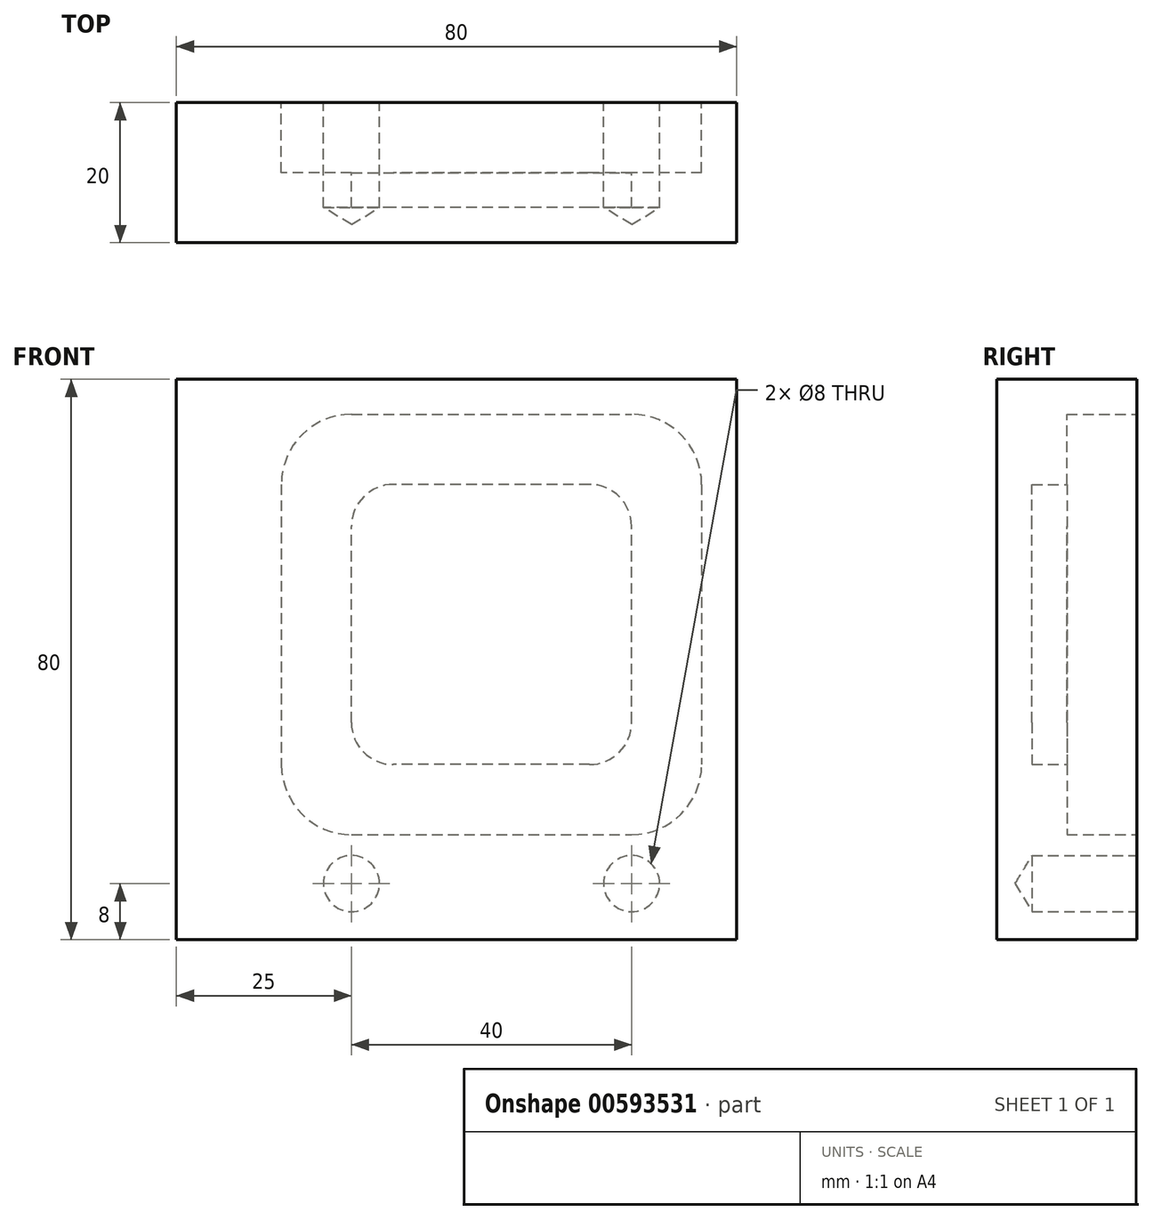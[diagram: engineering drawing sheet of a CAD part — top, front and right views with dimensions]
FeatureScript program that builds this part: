
annotation { "Feature Type Name" : "Feature", "Feature Type Description" : "" }
export const myFeature = defineFeature(function(context is Context, id is Id, definition is map)
    precondition{}
    {
        {
            var Q0;
            Q0=qCreatedBy(makeId("Front.planeOp"),FACE);
            var sketch = newSketch(context, id + "F0", { "sketchPlane" : qUnion([Q0])});
            skLineSegment(sketch, "E0", {"start": v(40, -40) * mm, "end": v(40, 40) * mm});
            skLineSegment(sketch, "E1", {"start": v(40, 40) * mm, "end": v(-40, 40) * mm});
            skLineSegment(sketch, "E2", {"start": v(-40, 40) * mm, "end": v(-40, -40) * mm});
            skLineSegment(sketch, "E3", {"start": v(-40, -40) * mm, "end": v(40, -40) * mm});
            skSolve(sketch);
        }
        {
            var Q0;
            Q0 = qSketchRegion(id + "F0", true);
            extrude(context, id + "F1", {"entities" : qUnion([Q0]), "depth" : 20 * mm, "offsetDistance" : 25 * mm});
        }
        {
            var Q0;
            Q0=makeQuery(id+"F1.opExtrude","CAP_FACE",FACE,{"disambiguationData":[OSD([sQuery(id+"F0.wireOp",EDGE,"E0"),sQuery(id+"F0.wireOp",EDGE,"E1"),sQuery(id+"F0.wireOp",EDGE,"E2"),sQuery(id+"F0.wireOp",EDGE,"E3")])],"isStart":true});
            var sketch = newSketch(context, id + "F2", { "sketchPlane" : qUnion([Q0])});
            skCircle(sketch, "E4", {"center": v(-25, -32) * mm, "radius": 4 * mm});
            skCircle(sketch, "E5", {"center": v(15, -32) * mm, "radius": 4 * mm});
            skSolve(sketch);
        }
        {
            var Q0;
            Q0=sQuery(id+"F2.wireOp",VERTEX,"E4.center");
            var Q1;
            Q1=sQuery(id+"F2.wireOp",VERTEX,"E5.center");
            var Q2;
            Q2=makeQuery(id+"F1.opExtrude","SWEPT_BODY",BODY,{"disambiguationData":[OSD([sQuery(id+"F0.wireOp",EDGE,"E0"),sQuery(id+"F0.wireOp",EDGE,"E1"),sQuery(id+"F0.wireOp",EDGE,"E2"),sQuery(id+"F0.wireOp",EDGE,"E3")])]});
            hole(context, id + "F3", {"style" : HoleStyle.SIMPLE, "endStyle" : HoleEndStyle.BLIND, "holeDiameter" : 8 * mm, "majorDiameter" : 5 * mm, "holeDepth" : 15 * mm, "isTappedThrough" : true, "tappedDepth" : 12 * mm, "tapClearance" : 3, "locations" : qUnion([Q0, Q1]), "scope" : qUnion([Q2])});
        }
        {
            var Q0;
            Q0=makeQuery(id+"F1.opExtrude","CAP_FACE",FACE,{"disambiguationData":[OSD([sQuery(id+"F0.wireOp",EDGE,"E0"),sQuery(id+"F0.wireOp",EDGE,"E1"),sQuery(id+"F0.wireOp",EDGE,"E2"),sQuery(id+"F0.wireOp",EDGE,"E3")])],"isStart":true});
            var sketch = newSketch(context, id + "F4", { "sketchPlane" : qUnion([Q0])});
            skPoint(sketch, "E6.middle", {"position": v(0, 0) * mm});
            skLineSegment(sketch, "E7.bottom", {"start": v(15, 35) * mm, "end": v(-25, 35) * mm});
            skLineSegment(sketch, "E7.top", {"start": v(15, -25) * mm, "end": v(-25, -25) * mm});
            skLineSegment(sketch, "E7.left", {"start": v(25, 25) * mm, "end": v(25, -15) * mm});
            skLineSegment(sketch, "E7.right", {"start": v(-35, 25) * mm, "end": v(-35, -15) * mm});
            skPoint(sketch, "E7.middle", {"position": v(-5, 5) * mm});
            skPoint(sketch, "E8.visualSharp", {"position": v(-35, 35) * mm});
            skArc(sketch, "E8.filletArc", {"start": v(-25, 35) * mm, "mid": v(-32.07, 32.07) * mm, "end": v(-35, 25) * mm});
            skPoint(sketch, "E9.visualSharp", {"position": v(-35, -25) * mm});
            skArc(sketch, "E9.filletArc", {"start": v(-35, -15) * mm, "mid": v(-32.07, -22.07) * mm, "end": v(-25, -25) * mm});
            skPoint(sketch, "E10.visualSharp", {"position": v(25, -25) * mm});
            skArc(sketch, "E10.filletArc", {"start": v(15, -25) * mm, "mid": v(22.07, -22.07) * mm, "end": v(25, -15) * mm});
            skPoint(sketch, "E11.visualSharp", {"position": v(25, 35) * mm});
            skArc(sketch, "E11.filletArc", {"start": v(25, 25) * mm, "mid": v(22.07, 32.07) * mm, "end": v(15, 35) * mm});
            skSolve(sketch);
        }
        {
            var Q0;
            Q0 = qSketchRegion(id + "F4", true);
            extrude(context, id + "F5", {"entities" : qUnion([Q0]), "operationType" : NewBodyOperationType.REMOVE, "oppositeDirection" : true, "depth" : 10 * mm, "offsetDistance" : 25 * mm});
        }
        {
            var Q0;
            Q0=makeQuery(id+"F5.boolean.opBoolean","COPY",FACE,{"derivedFrom":makeQuery(id+"F5.opExtrude","CAP_FACE",FACE,{"disambiguationData":[OSD([sQuery(id+"F4.wireOp",EDGE,"E7.bottom"),sQuery(id+"F4.wireOp",EDGE,"E7.top"),sQuery(id+"F4.wireOp",EDGE,"E7.left"),sQuery(id+"F4.wireOp",EDGE,"E7.right"),sQuery(id+"F4.wireOp",EDGE,"E8.filletArc"),sQuery(id+"F4.wireOp",EDGE,"E9.filletArc"),sQuery(id+"F4.wireOp",EDGE,"E10.filletArc"),sQuery(id+"F4.wireOp",EDGE,"E11.filletArc")])],"isStart":false})});
            var sketch = newSketch(context, id + "F6", { "sketchPlane" : qUnion([Q0])});
            skLineSegment(sketch, "E12.bottom", {"start": v(-19, -15) * mm, "end": v(9, -15) * mm});
            skLineSegment(sketch, "E12.top", {"start": v(-19, 25) * mm, "end": v(9, 25) * mm});
            skLineSegment(sketch, "E12.left", {"start": v(-25, -9) * mm, "end": v(-25, 19) * mm});
            skLineSegment(sketch, "E12.right", {"start": v(15, -9) * mm, "end": v(15, 19) * mm});
            skPoint(sketch, "E12.middle", {"position": v(-5, 5) * mm});
            skPoint(sketch, "E13.visualSharp", {"position": v(-25, 25) * mm});
            skArc(sketch, "E13.filletArc", {"start": v(-19, 25) * mm, "mid": v(-23.24, 23.24) * mm, "end": v(-25, 19) * mm});
            skPoint(sketch, "E14.visualSharp", {"position": v(-25, -15) * mm});
            skArc(sketch, "E14.filletArc", {"start": v(-25, -9) * mm, "mid": v(-23.24, -13.24) * mm, "end": v(-19, -15) * mm});
            skPoint(sketch, "E15.visualSharp", {"position": v(15, -15) * mm});
            skArc(sketch, "E15.filletArc", {"start": v(9, -15) * mm, "mid": v(13.24, -13.24) * mm, "end": v(15, -9) * mm});
            skPoint(sketch, "E16.visualSharp", {"position": v(15, 25) * mm});
            skArc(sketch, "E16.filletArc", {"start": v(15, 19) * mm, "mid": v(13.24, 23.24) * mm, "end": v(9, 25) * mm});
            skSolve(sketch);
        }
        {
            var Q0;
            Q0 = qSketchRegion(id + "F6", true);
            extrude(context, id + "F7", {"entities" : qUnion([Q0]), "operationType" : NewBodyOperationType.REMOVE, "oppositeDirection" : true, "depth" : 5 * mm, "offsetDistance" : 25 * mm});
        }
    });
